# Revit family: Atdec-Wallmount-AD-WF50-Landscape-
name_source: partatom
category: Generic Models
revit_build: Autodesk Revit 2016 (Build: 20150220_1215(x64)
units: mm (PartAtom-declared; Revit-internal decimal feet)

## family parameters
Can host rebar = No
Cut with Voids When Loaded = No
Host = Face
Part Type = Normal
Room Calculation Point = No
Round Connector Dimension = Use Diameter
Shared = No

## types (2) — shared parameters
Assembly Code = E1010800
Colour Options = Black
Default Elevation = 1219 mm
Flat screen maximum supported weight = 50kg (110lb)
Manufacturer = Atdec
Material = Steel
Maximum distance from wall (mm) = 25mm (0.98")
Minimum distance from wall (mm) = 25mm (0.98")
Pan Adjustment = -
Product Family = Wall Mount Rail
Product Information Link = https://www.atdec.com.au
Range of Motion = Fixed Angle
Security feature = -
Tilt Adjustment = -
URL = www.atdec.com.au
Warranty = 10 years

## per-type parameters (varying)
| type | Description | Master Carton Dimensions | Plate Width | Single Unit Dimensions | Single units per master pack | UPC Code | Universal Height (mm) | Universal Width (mm) | VESA mounting hole pattern, mm | Weight, Single Unit | Weight, master carton |
| AD-WF-5040 | Fixed angle wall mount VESA up to 400x400 | 480mm (18.9") Length, 205mm (8.1") Width, 330mm (13") Height | 448 mm  [stored 1.46982 ft] | 465mm (18.3") Length, 155mm (6.1") Width, 30mm (1.2") Height | 12 | 881493019157 | From 100 to 400 | From 100 to 400 | 100x100, 100x200, 200x100, 200x200, 200x300, 200x400, 300x200, 300x300, 400x200, 400x300, 400x400 | 1.58 (3.48lb) | 19.35kg (42.66lb) |
| AD-WF-5060 | Fixed angle wall mount VESA up to 600x600 | 685mm (27") Length, 265mm (10.4") Width, 170mm (6.7") Height | 653 mm  [stored 2.14239 ft] | 670mm (26.4") Length, 155mm (6.1") Width, 30mm (1.2") Height | 18 | 881493019171 | From 100 to 600 | From 100 to 600 | 100x100, 100x200, 200x100, 200x200, 200x300, 200x400, 300x200, 300x300, 400x200, 400x300, 400x400, 600x200, 600x400 | 1.98 (4.37lb) | 16.38kg (36.11lb) |

note: column(s) folded — value = type name in every type: Model

note: [stored X ft] marks values corroborated as IEEE doubles in the binary element streams (Revit-internal decimal feet)

## geometry (parser evidence)
native form markers: Sweep x2
no freeform markers — native parametric forms only
